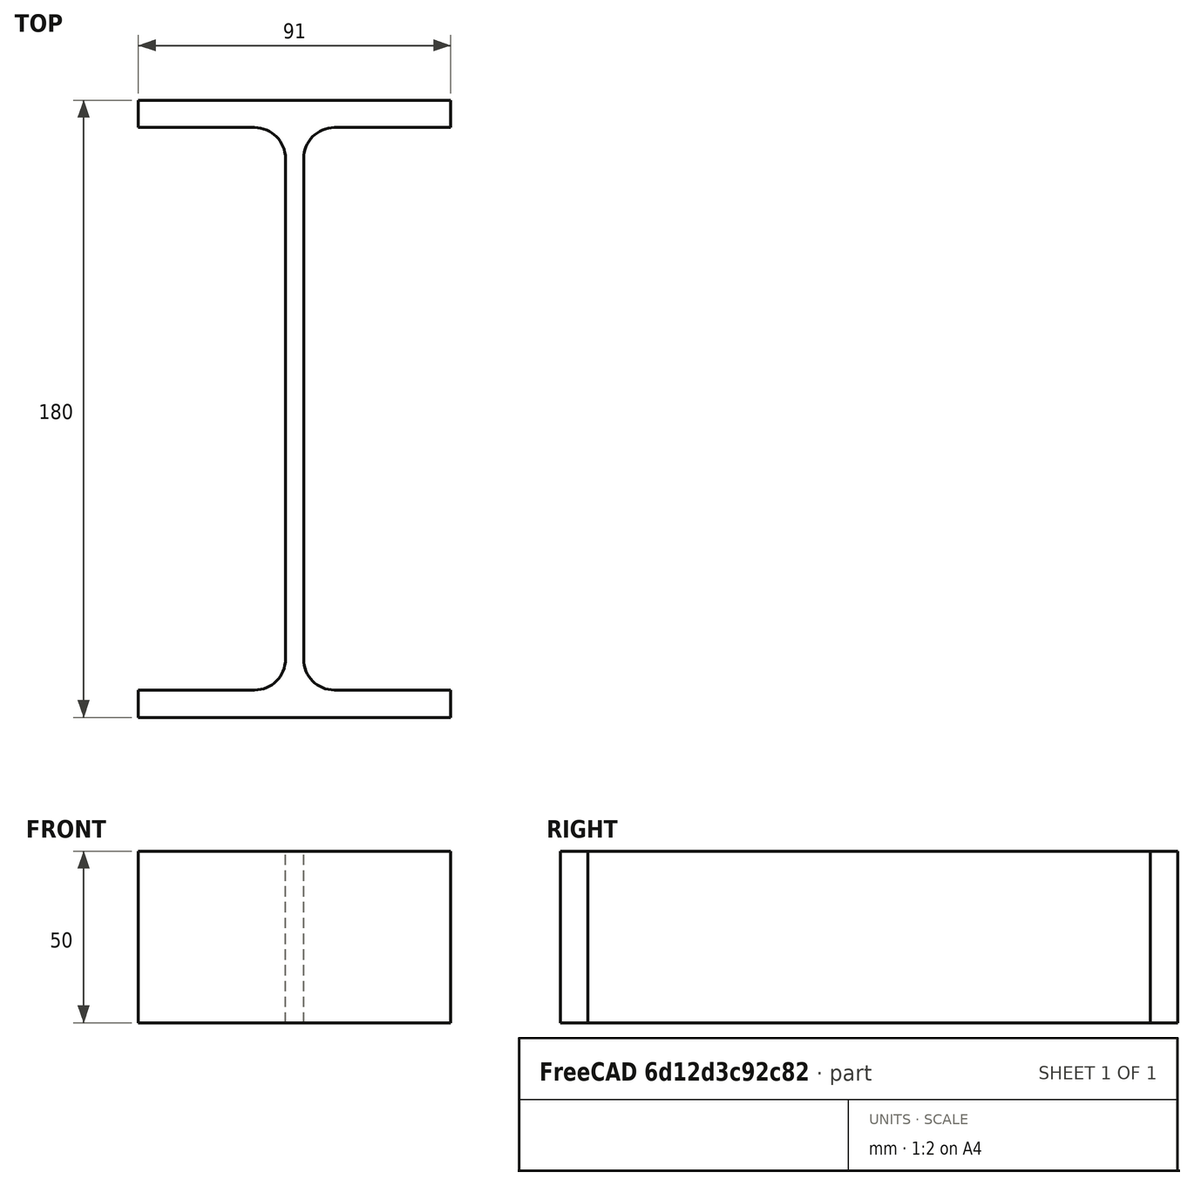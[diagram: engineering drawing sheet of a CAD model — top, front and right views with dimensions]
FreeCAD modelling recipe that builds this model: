
FCSTD DOCUMENT  (FreeCAD 0.15R4671 (Git))
Label: IPE-Profile 180 DIN1025-5 S235JR
License: All rights reserved
LicenseURL: http://en.wikipedia.org/wiki/All_rights_reserved
objects: Sketcher::SketchObject×1, Part::Extrusion×1
note: 2 computed .brp shape members not serialized (recipe doc carries the construction recipe); baked Part::Feature solids carry a one-line shape summary decoded from their .brp

FEATURE [Sketcher::SketchObject] Sketch
  sketch-geometry (16):
    g0: LineSegment StartX=2.65 StartY=-73 StartZ=0 EndX=2.65 EndY=73 EndZ=0
    g1: LineSegment StartX=11.65 StartY=82 StartZ=0 EndX=45.5 EndY=82 EndZ=0
    g2: LineSegment StartX=45.5 StartY=82 StartZ=0 EndX=45.5 EndY=90 EndZ=0
    g3: LineSegment StartX=45.5 StartY=90 StartZ=0 EndX=-45.5 EndY=90 EndZ=0
    g4: LineSegment StartX=-45.5 StartY=90 StartZ=0 EndX=-45.5 EndY=82 EndZ=0
    g5: LineSegment StartX=-45.5 StartY=82 StartZ=0 EndX=-11.65 EndY=82 EndZ=0
    g6: LineSegment StartX=-2.65 StartY=73 StartZ=0 EndX=-2.65 EndY=-73 EndZ=0
    g7: LineSegment StartX=-11.65 StartY=-82 StartZ=0 EndX=-45.5 EndY=-82 EndZ=0
    g8: LineSegment StartX=-45.5 StartY=-82 StartZ=0 EndX=-45.5 EndY=-90 EndZ=0
    g9: LineSegment StartX=-45.5 StartY=-90 StartZ=0 EndX=45.5 EndY=-90 EndZ=0
    g10: LineSegment StartX=45.5 StartY=-90 StartZ=0 EndX=45.5 EndY=-82 EndZ=0
    g11: LineSegment StartX=45.5 StartY=-82 StartZ=0 EndX=11.65 EndY=-82 EndZ=0
    g12: ArcOfCircle CenterX=11.65 CenterY=73 CenterZ=0 NormalX=0 NormalY=0 NormalZ=1 Radius=9 StartAngle=1.5708 EndAngle=3.14159
    g13: ArcOfCircle CenterX=11.65 CenterY=-73 CenterZ=0 NormalX=0 NormalY=0 NormalZ=1 Radius=9 StartAngle=3.14159 EndAngle=4.71239
    g14: ArcOfCircle CenterX=-11.65 CenterY=73 CenterZ=0 NormalX=0 NormalY=0 NormalZ=1 Radius=9 StartAngle=0 EndAngle=1.5708
    g15: ArcOfCircle CenterX=-11.65 CenterY=-73 CenterZ=0 NormalX=0 NormalY=0 NormalZ=1 Radius=9 StartAngle=4.71239 EndAngle=6.28319
  constraints (42):
    c: Vertical(g0)
    c: Coincident(g2,g1)
    c: Vertical(g2)
    c: Coincident(g3,g2)
    c: Coincident(g4,g3)
    c: Vertical(g4)
    c: Coincident(g5,g4)
    c: Horizontal(g5)
    c: Vertical(g6)
    c: Horizontal(g7)
    c: Coincident(g8,g7)
    c: Vertical(g8)
    c: Coincident(g9,g8)
    c: Horizontal(g9)
    c: Coincident(g10,g9)
    c: Vertical(g10)
    c: Coincident(g11,g10)
    c: Horizontal(g11)
    c: Tangent(g1,g12) = 1.5708
    c: Tangent(g0,g12) = 1.5708
    c: Tangent(g0,g13) = 1.5708
    c: Tangent(g11,g13) = 1.5708
    c: Tangent(g5,g14) = 1.5708
    c: Tangent(g6,g14) = 1.5708
    c: Tangent(g6,g15) = 1.5708
    c: Tangent(g7,g15) = 1.5708
    c: Equal(g3,g9)
    c: Equal(g2,g4)
    c: Equal(g4,g8)
    c: Equal(g8,g10)
    c: Equal(g12,g14)
    c: Equal(g14,g15)
    c: Equal(g15,g13)
    c: Symmetric(g2,g3,g-2)
    c: Symmetric(g9,g8,g-2)
    c: Symmetric(g0,g6,g-2)
    c: Symmetric(g2,g9,g-1)
    c: DistanceY(g2,g9) = -180
    c: DistanceX(g3) = -91
    c: DistanceX(g0,g6) = -5.3
    c: DistanceY(g2) = 8
    c: Radius(g12) = 9
FEATURE [Part::Extrusion] Extrude  label="IPE-Profile 180 DIN1025-5 S235JR"
  Base = -> Sketch
  Dir = (0,0,50)
  Solid = true
